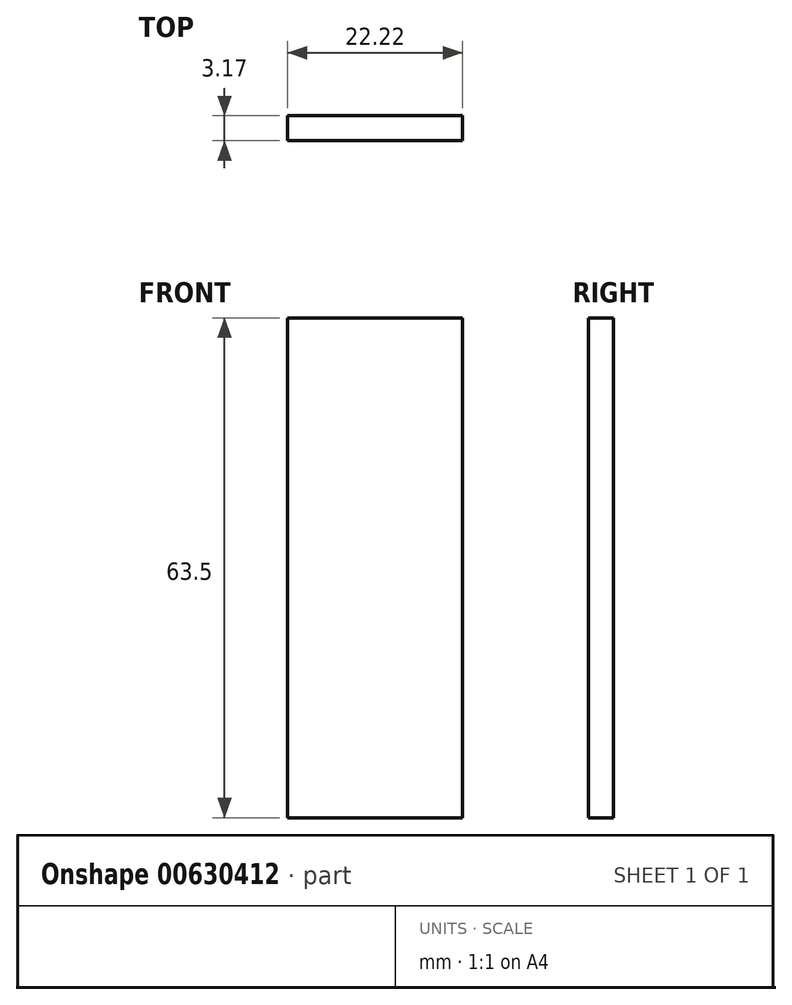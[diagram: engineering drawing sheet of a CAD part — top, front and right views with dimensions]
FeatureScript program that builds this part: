
annotation { "Feature Type Name" : "Feature", "Feature Type Description" : "" }
export const myFeature = defineFeature(function(context is Context, id is Id, definition is map)
    precondition{}
    {
        {
            var Q0;
            Q0=qCreatedBy(makeId("Front.planeOp"),FACE);
            var sketch = newSketch(context, id + "F0", { "sketchPlane" : qUnion([Q0])});
            skLineSegment(sketch, "E0.bottom", {"start": v(11.11, 31.75) * mm, "end": v(-11.11, 31.75) * mm});
            skLineSegment(sketch, "E0.top", {"start": v(11.11, -31.75) * mm, "end": v(-11.11, -31.75) * mm});
            skLineSegment(sketch, "E0.left", {"start": v(11.11, 31.75) * mm, "end": v(11.11, -31.75) * mm});
            skLineSegment(sketch, "E0.right", {"start": v(-11.11, 31.75) * mm, "end": v(-11.11, -31.75) * mm});
            skPoint(sketch, "E0.middle", {"position": v(0, 0) * mm});
            skSolve(sketch);
        }
        {
            var Q0;
            Q0=qSketchRegion(id+"F0",true);
            extrude(context, id + "F1", {"entities" : qUnion([Q0]), "depth" : 3.17 * mm, "offsetDistance" : 25.4 * mm});
        }
    });
